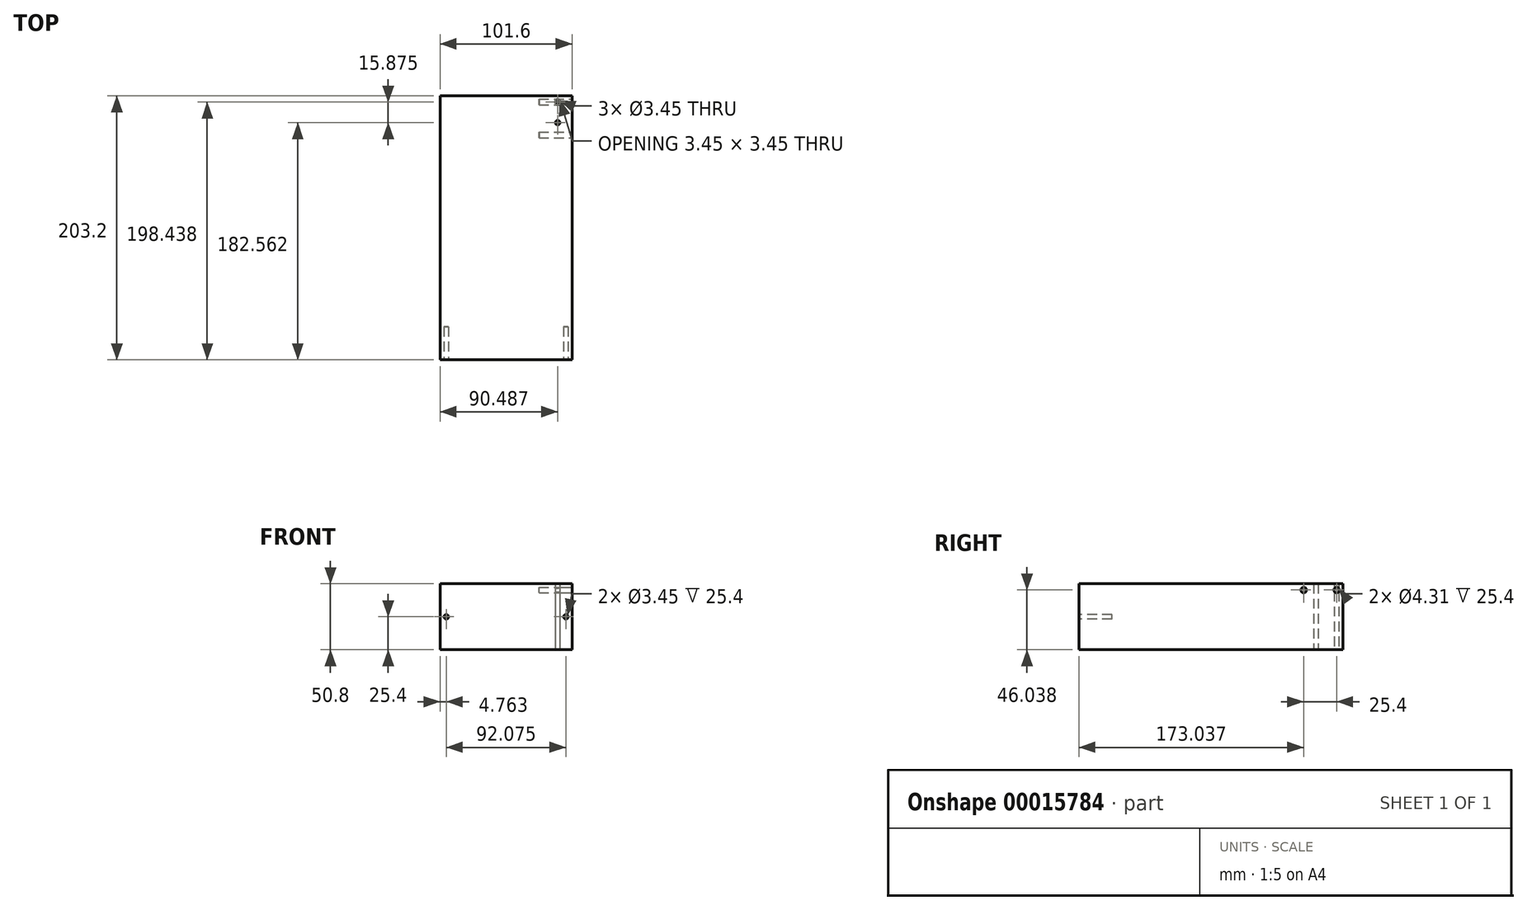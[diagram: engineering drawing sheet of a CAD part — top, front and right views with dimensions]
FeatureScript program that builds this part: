
annotation { "Feature Type Name" : "Feature", "Feature Type Description" : "" }
export const myFeature = defineFeature(function(context is Context, id is Id, definition is map)
    precondition{}
    {
        {
            var Q0;
            Q0=qCreatedBy(makeId("Top.planeOp"),FACE);
            var sketch = newSketch(context, id + "F0", { "sketchPlane" : qUnion([Q0])});
            skLineSegment(sketch, "E0.bottom", {"start": v(0, 0) * mm, "end": v(101.6, 0) * mm});
            skLineSegment(sketch, "E0.top", {"start": v(0, -203.2) * mm, "end": v(101.6, -203.2) * mm});
            skLineSegment(sketch, "E0.left", {"start": v(0, 0) * mm, "end": v(0, -203.2) * mm});
            skLineSegment(sketch, "E0.right", {"start": v(101.6, 0) * mm, "end": v(101.6, -203.2) * mm});
            skLineSegment(sketch, "E1", {"start": v(90.49, 0) * mm, "end": v(90.49, -4.76) * mm, "construction": true});
            skLineSegment(sketch, "E2", {"start": v(90.49, -4.76) * mm, "end": v(101.6, -4.76) * mm, "construction": true});
            skLineSegment(sketch, "E3", {"start": v(90.49, -4.76) * mm, "end": v(90.49, -20.64) * mm, "construction": true});
            skCircle(sketch, "E4", {"center": v(90.49, -4.76) * mm, "radius": 1.73 * mm});
            skCircle(sketch, "E5", {"center": v(90.49, -20.64) * mm, "radius": 1.73 * mm});
            skSolve(sketch);
        }
        {
            var Q0;
            Q0 = qSketchRegion(id + "F0", true);
            extrude(context, id + "F1", {"entities" : qUnion([Q0]), "depth" : 50.8 * mm});
        }
        {
            var Q0;
            Q0=makeQuery(id+"F1.opExtrude","SWEPT_FACE",FACE,{"disambiguationData":[OSD([sQuery(id+"F0.wireOp",EDGE,"E0.top")])]});
            var sketch = newSketch(context, id + "F2", { "sketchPlane" : qUnion([Q0])});
            skLineSegment(sketch, "E6", {"start": v(0, 25.4) * mm, "end": v(4.76, 25.4) * mm});
            skLineSegment(sketch, "E7", {"start": v(4.76, 25.4) * mm, "end": v(96.84, 25.4) * mm});
            skLineSegment(sketch, "E8", {"start": v(96.84, 25.4) * mm, "end": v(101.6, 25.4) * mm});
            skCircle(sketch, "E9", {"center": v(96.84, 25.4) * mm, "radius": 1.73 * mm});
            skCircle(sketch, "E10", {"center": v(4.76, 25.4) * mm, "radius": 1.73 * mm});
            skSolve(sketch);
        }
        {
            var Q0;
            Q0 = qSketchRegion(id + "F2", true);
            extrude(context, id + "F3", {"entities" : qUnion([Q0]), "operationType" : NewBodyOperationType.REMOVE, "oppositeDirection" : true, "depth" : 25.4 * mm});
        }
        {
            var Q0;
            Q0=makeQuery(id+"F1.opExtrude","SWEPT_FACE",FACE,{"disambiguationData":[OSD([sQuery(id+"F0.wireOp",EDGE,"E0.right")])]});
            var sketch = newSketch(context, id + "F4", { "sketchPlane" : qUnion([Q0])});
            skLineSegment(sketch, "E11", {"start": v(-4.76, 50.8) * mm, "end": v(-4.76, 46.04) * mm, "construction": true});
            skLineSegment(sketch, "E12", {"start": v(-4.76, 46.04) * mm, "end": v(0, 46.04) * mm, "construction": true});
            skCircle(sketch, "E13", {"center": v(-4.76, 46.04) * mm, "radius": 2.15 * mm});
            skLineSegment(sketch, "E14", {"start": v(-4.76, 46.04) * mm, "end": v(-30.16, 46.04) * mm, "construction": true});
            skCircle(sketch, "E15", {"center": v(-30.16, 46.04) * mm, "radius": 2.15 * mm});
            skSolve(sketch);
        }
        {
            var Q0;
            Q0 = qSketchRegion(id + "F4", true);
            extrude(context, id + "F5", {"entities" : qUnion([Q0]), "operationType" : NewBodyOperationType.REMOVE, "oppositeDirection" : true, "depth" : 25.4 * mm});
        }
    });
